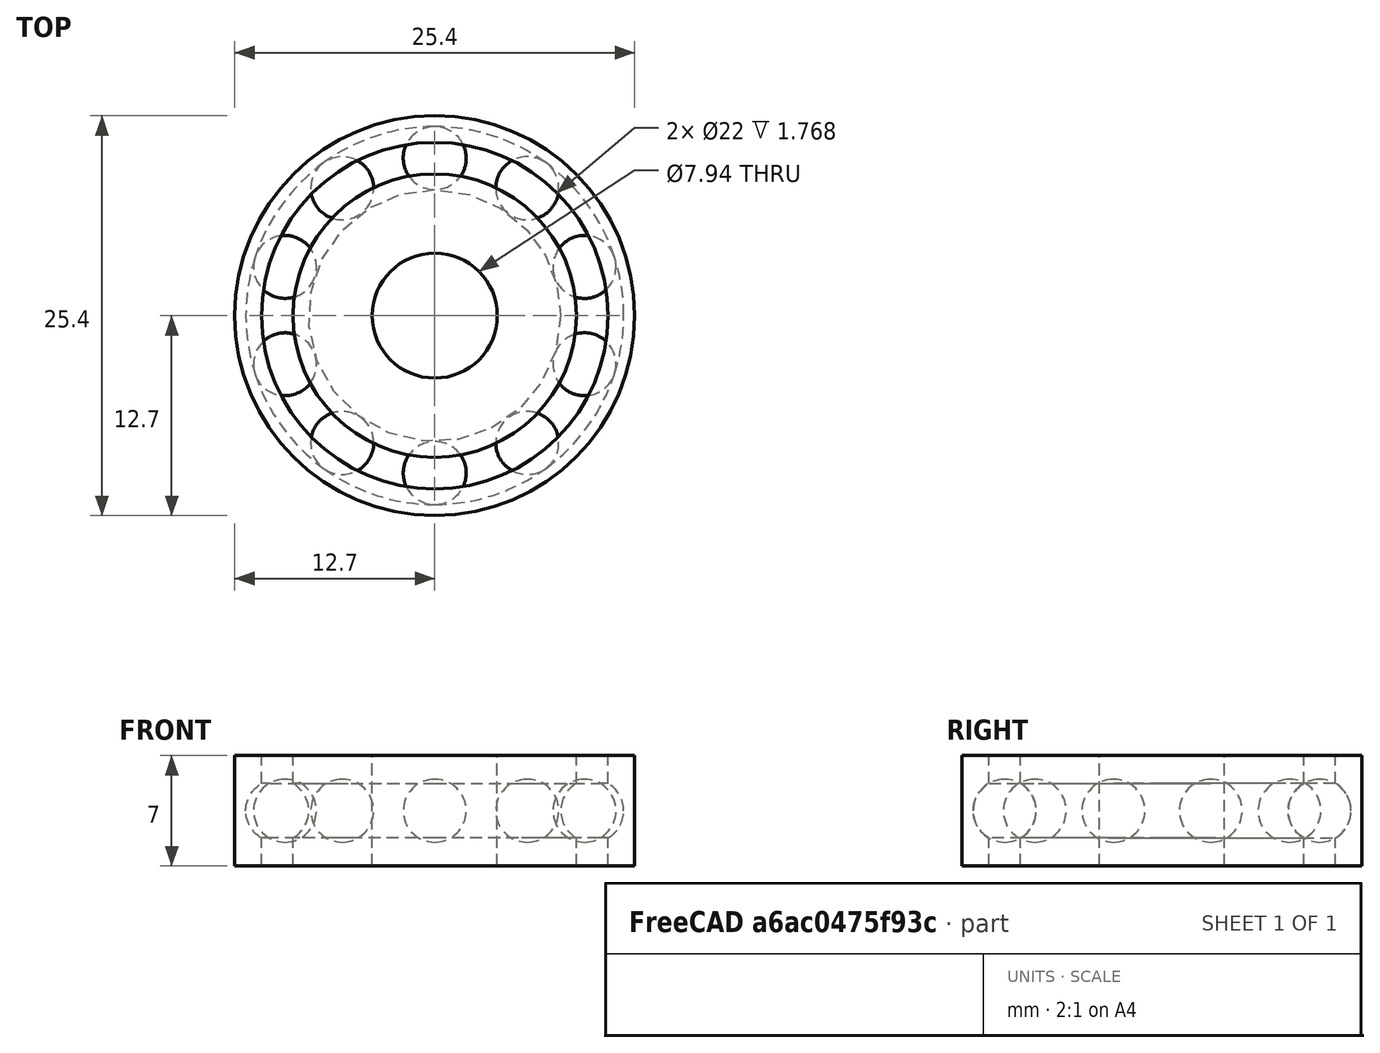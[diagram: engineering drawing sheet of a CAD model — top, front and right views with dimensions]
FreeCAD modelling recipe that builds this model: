
FCSTD DOCUMENT  (FreeCAD 0.18.4R)
Label: baleroCHIDO
License: All rights reserved
LicenseURL: http://en.wikipedia.org/wiki/All_rights_reserved
objects: Part::Cylinder×4, Part::Cut×3, Part::Torus×1, Part::Fuse×1, Part::Sphere×1, Part::FeaturePython×1, Part::MultiFuse×1
note: 12 computed .brp shape members not serialized (recipe doc carries the construction recipe); baked Part::Feature solids carry a one-line shape summary decoded from their .brp

FEATURE [Part::Cylinder] Cylinder  label="Cilindro"
  Angle = 360
  AttacherType = Attacher::AttachEngine3D
  Height = 7
  Radius = 12.7
FEATURE [Part::Cylinder] Cylinder001  label="Cilindro001"
  Angle = 360
  AttacherType = Attacher::AttachEngine3D
  Height = 7
  Radius = 11
FEATURE [Part::Cylinder] Cylinder002  label="Cilindro002"
  Angle = 360
  AttacherType = Attacher::AttachEngine3D
  Height = 7
  Radius = 3.96875
FEATURE [Part::Cylinder] Cylinder003  label="Cilindro003"
  Angle = 360
  AttacherType = Attacher::AttachEngine3D
  Height = 7
  Radius = 9
FEATURE [Part::Cut] Cut
  Base = -> Cylinder
  Tool = -> Cylinder001
FEATURE [Part::Cut] Cut001
  Base = -> Cylinder003
  Tool = -> Cylinder002
FEATURE [Part::Torus] Torus  label="Toro"
  Angle1 = -180
  Angle2 = 180
  Angle3 = 360
  AttacherType = Attacher::AttachEngine3D
  Placement = pos=(0,0,3.5) rot=(0,0,1;0rad)
  Radius1 = 10
  Radius2 = 2
FEATURE [Part::Fuse] Fusion
  Base = -> Cut
  Tool = -> Cut001
FEATURE [Part::Cut] Cut002
  Base = -> Fusion
  Tool = -> Torus
FEATURE [Part::Sphere] Sphere  label="Esfera"
  Angle1 = -90
  Angle2 = 90
  Angle3 = 360
  AttacherType = Attacher::AttachEngine3D
  Placement = pos=(0,10,3.5) rot=(0,0,1;0rad)
  Radius = 2
FEATURE [Part::FeaturePython] Array  # Draft array (typed FeaturePython)
  Angle = 360
  ArrayType = 1
  Axis = (0,0,1)
  Base = -> Sphere
  Center = (0,0,0)
  Fuse = false
  IntervalAxis = (0,0,0)
  IntervalX = (1,0,0)
  IntervalY = (0,1,0)
  IntervalZ = (0,0,1)
  NumberPolar = 10
  NumberX = 2
  NumberY = 2
  NumberZ = 1
FEATURE [Part::MultiFuse] Fusion001
  Shapes = -> [Cut002,Array]
